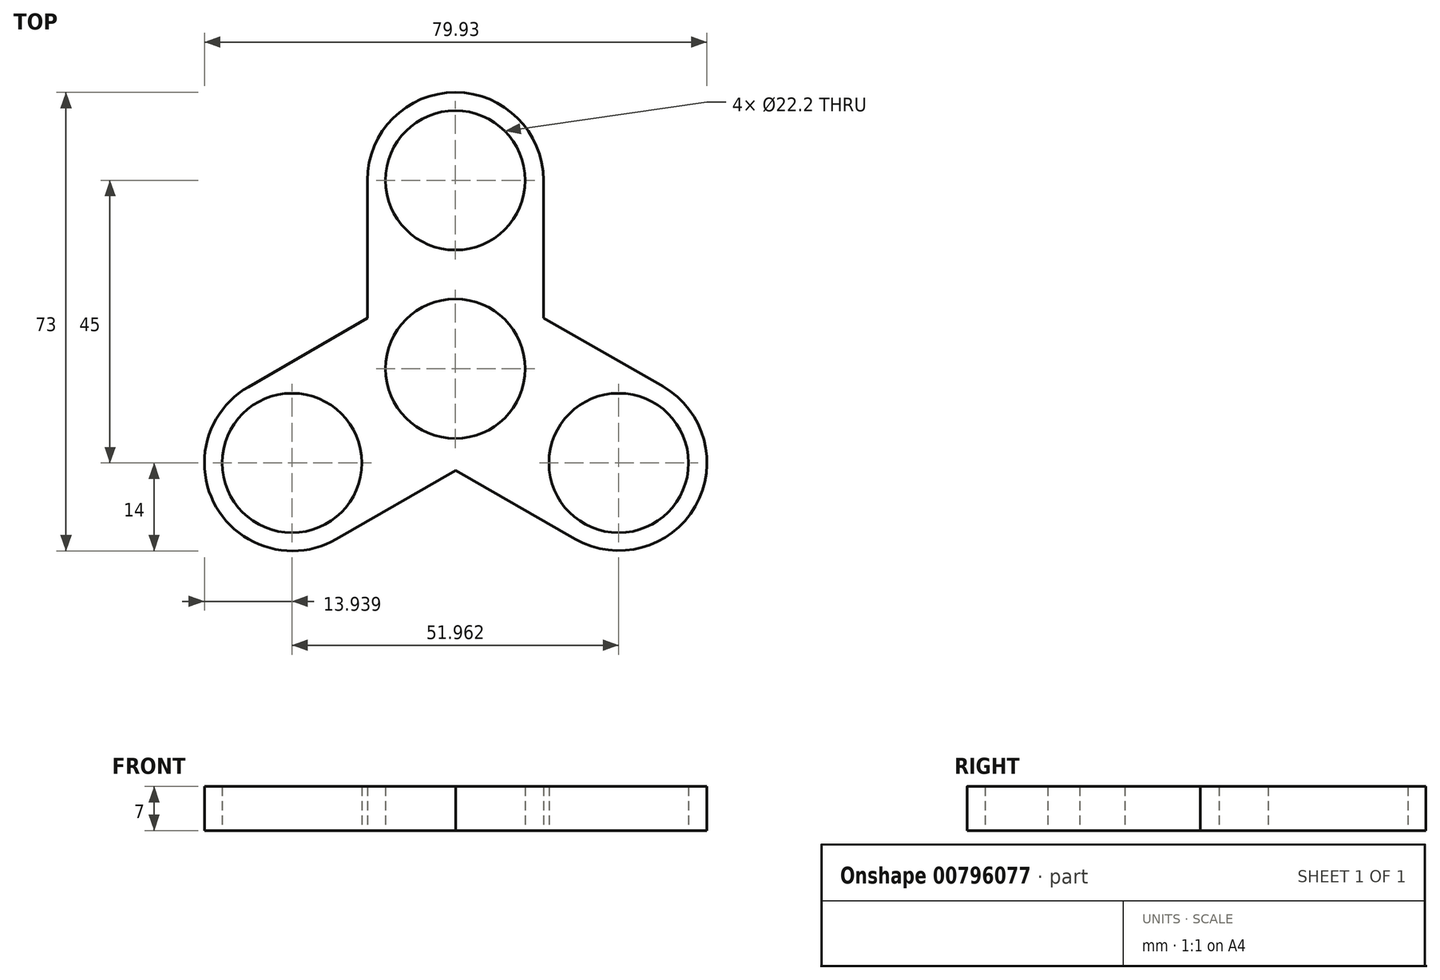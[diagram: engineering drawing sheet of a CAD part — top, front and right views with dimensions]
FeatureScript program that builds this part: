
annotation { "Feature Type Name" : "Feature", "Feature Type Description" : "" }
export const myFeature = defineFeature(function(context is Context, id is Id, definition is map)
    precondition{}
    {
        {
            var Q0;
            Q0=qCreatedBy(makeId("Top.planeOp"),FACE);
            var sketch = newSketch(context, id + "F0", { "sketchPlane" : qUnion([Q0])});
            skCircle(sketch, "E0", {"center": v(0, 0) * mm, "radius": 11.1 * mm});
            skCircle(sketch, "E1", {"center": v(0, 30) * mm, "radius": 11.1 * mm});
            skArc(sketch, "E2", {"start": v(14, 30) * mm, "mid": v(0, 44) * mm, "end": v(-14, 30) * mm});
            skArc(sketch, "E3.1.0", {"start": v(-32.93, -2.88) * mm, "mid": v(-38.04, -22.01) * mm, "end": v(-18.9, -27.12) * mm});
            skArc(sketch, "E3.2.0", {"start": v(19.04, -27.09) * mm, "mid": v(38.15, -21.92) * mm, "end": v(32.99, -2.8) * mm});
            skPoint(sketch, "E3.center", {"position": v(0.03, 0.02) * mm});
            skCircle(sketch, "E4.1.0", {"center": v(-25.98, -15) * mm, "radius": 11.1 * mm});
            skCircle(sketch, "E4.2.0", {"center": v(25.98, -15) * mm, "radius": 11.1 * mm});
            skLineSegment(sketch, "E5", {"start": v(-32.93, -2.88) * mm, "end": v(-14, 8.07) * mm});
            skLineSegment(sketch, "E6", {"start": v(-18.9, -27.12) * mm, "end": v(0.02, -16.16) * mm});
            skLineSegment(sketch, "E7", {"start": v(14, 30) * mm, "end": v(14, 8.1) * mm});
            skLineSegment(sketch, "E8", {"start": v(-14, 30) * mm, "end": v(-14, 8.07) * mm});
            skLineSegment(sketch, "E9", {"start": v(0.02, -16.16) * mm, "end": v(19.04, -27.09) * mm});
            skLineSegment(sketch, "E10", {"start": v(14, 8.1) * mm, "end": v(32.99, -2.8) * mm});
            skSolve(sketch);
        }
        {
            var Q0;
            Q0=makeQuery(id+"F0.imprint","IMPRINT",FACE,{"disambiguationData":[TD([[makeQuery(id+"F0.imprint","IMPRINT",EDGE,{"derivedFrom":sQuery(id+"F0.wireOp",EDGE,"E0")}),-1.0]])]});
            extrude(context, id + "F1", {"entities" : qUnion([Q0]), "endBound" : BoundingType.SYMMETRIC, "depth" : 7 * mm, "offsetDistance" : 25 * mm});
        }
    });
